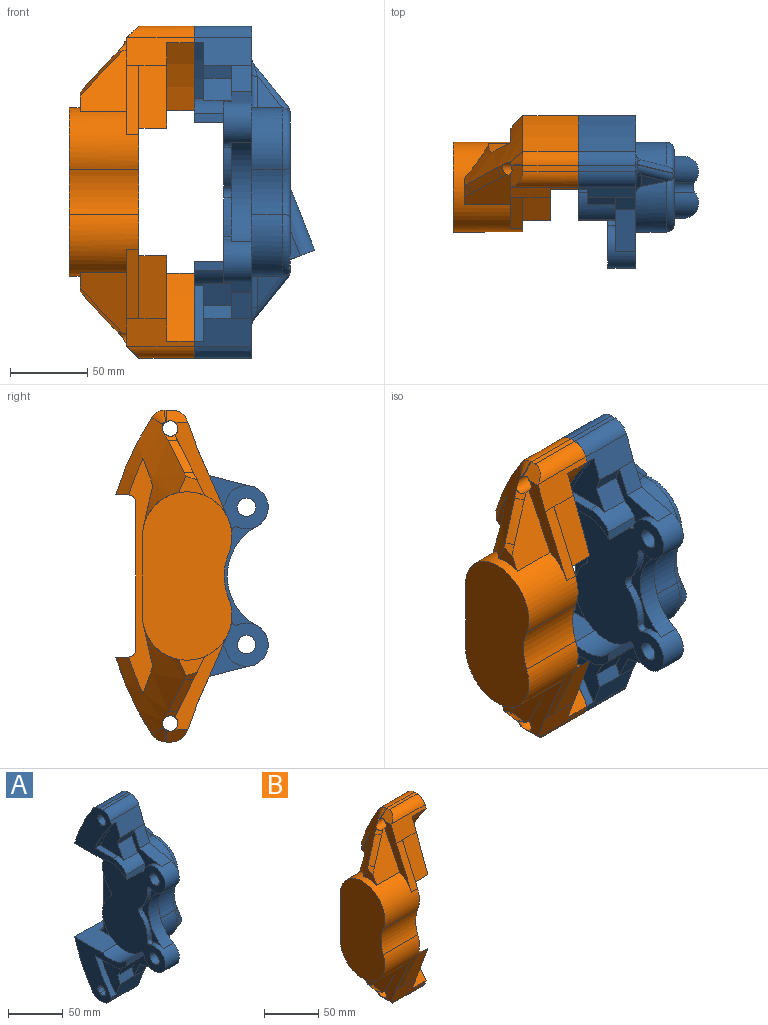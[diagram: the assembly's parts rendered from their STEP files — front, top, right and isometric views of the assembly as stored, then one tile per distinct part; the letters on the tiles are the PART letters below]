
ASSEMBLY  parts=2 mates=1
PART A: 111 faces, bbox 78.4x99.2x215.6 mm
  f0: plane 0.16x0.1mm, normal (1,0,0), area 0mm2, adj f5,f6,f106
  f1: plane 11.19x6.2mm, normal (1,0,0), area 44.8mm2, adj f2,f99,f105,f106
  f2: torus R=24mm, axis (1,0,0), area 416.6mm2, adj f1,f6,f7,f70,f76,f84,f86,f99
  f3: torus R=24mm, axis (1,0,0), area 209mm2, adj f4,f7,f8,f77,f82,f99,f101,f106
  f4: cylinder r=5mm len=4.92mm, axis (0,0.04,-1), area 9.5mm2, adj f3,f5,f77,f87,f106
  f5: cylinder r=5mm len=3.73mm, axis (0,-0.98,-0.19), area 5.6mm2, adj f0,f4,f6,f75,f86,f87,f106
  f6: cylinder r=5mm len=5.52mm, axis (0,0.34,-0.94), area 9.8mm2, adj f0,f2,f5,f86,f106
  f7: plane 90.46x48mm, normal (1,0,0), area 2353.6mm2, adj f2,f3,f78,f79,f80,f81,f82,f83
  f8: cylinder r=29mm len=25.69mm, axis (-1,0,0), area 582.4mm2, adj f3,f9,f71,f77,f89
  f9: plane 215x98.65mm, normal (1,0,0), area 5498.8mm2, adj f8,f10,f18,f19,f20,f21,f22,f23
  f10: cylinder r=29mm len=25.69mm, axis (-1,0,0), area 582.4mm2, adj f9,f71,f74,f80,f98
  f11: plane 37.95x37.12mm, normal (-1,0,0), area 306.6mm2, adj f44,f45,f46,f62,f63,f65,f66,f108
  f12: cylinder r=29mm len=48.75mm, axis (1,0,0), area 296.6mm2, adj f21,f28,f53,f54
  f13: extruded ~36.27x20.87mm, area 251.8mm2, adj f22,f27,f61,f67
  f14: cylinder r=159mm len=36.27mm, axis (-1,0,0), area 251.8mm2, adj f34,f36,f56,f60
  f15: cylinder r=20mm len=24mm, axis (1,0,0), area 348.4mm2, adj f16,f36,f56,f57,f58,f60
  f16: plane 37.95x37.12mm, normal (-1,0,0), area 306.6mm2, adj f15,f40,f41,f42,f57,f58,f59,f109
  f17: plane 64.37x27.62mm, normal (-1,0,0), area 336.7mm2, adj f42,f43,f44,f49,f50,f51,f107,f110
  f18: plane 37x3.51mm, normal (0,0,-1), area 130mm2, adj f9,f19,f26,f27
  f19: extruded ~37x9.16mm, area 400.7mm2, adj f9,f18,f20,f27
  f20: extruded ~50.09x37mm, area 2052.7mm2, adj f9,f19,f21,f27
  f21: plane 37x35.62mm, normal (0,0,1), area 958.8mm2, adj f9,f12,f20,f27,f28,f37,f64
  f22: plane 37x18.15mm, normal (0,-0.94,-0.34), area 621.1mm2, adj f9,f13,f26,f27,f46,f66,f67
  f23: extruded ~37x9.2mm, area 474.9mm2, adj f9,f24,f25,f27
  f24: extruded ~37x9.2mm, area 580.9mm2, adj f9,f23,f25,f27
  f25: extruded ~37x2.72mm, area 106.2mm2, adj f9,f23,f24,f27
  f26: extruded ~37x10.34mm, area 497.3mm2, adj f9,f18,f22,f27
  f27: plane 67.65x62.49mm, normal (-1,0,0), area 1567mm2, adj f13,f18,f19,f20,f21,f22,f23,f24
  f28: plane 105x27.62mm, normal (-1,0,0), area 938.6mm2, adj f12,f21,f29,f37,f38,f39,f52,f53
  f29: plane 37x35.62mm, normal (0,0,-1), area 958.8mm2, adj f9,f28,f30,f36,f39,f52,f55
  f30: cylinder r=185.44mm len=50.09mm, axis (-1,0,0), area 2052.7mm2, adj f9,f29,f31,f36
  f31: cylinder r=11mm len=37mm, axis (-1,0,0), area 400.7mm2, adj f9,f30,f32,f36
  f32: plane 37x3.51mm, normal (0,0,1), area 130mm2, adj f9,f31,f33,f36
  f33: cylinder r=11mm len=37mm, axis (-1,0,0), area 497.2mm2, adj f9,f32,f34,f36
  f34: plane 37x18.15mm, normal (0,-0.94,0.34), area 621.1mm2, adj f9,f14,f33,f36,f40,f59,f60
  f35: cylinder r=5mm len=37mm, axis (-1,0,0), area 1162.4mm2, adj f9,f36
  f36: plane 67.65x62.49mm, normal (-1,0,0), area 1567mm2, adj f14,f15,f29,f30,f31,f32,f33,f34
  f37: cylinder r=5mm len=13mm, axis (-1,0,0), area 102.1mm2, adj f9,f21,f28,f38
  f38: plane 95x13mm, normal (0,1,0), area 1235mm2, adj f9,f28,f37,f39
  f39: cylinder r=5mm len=13mm, axis (-1,0,0), area 102.1mm2, adj f9,f28,f29,f38
  f40: plane 17.18x13mm, normal (0,-0.92,0.4), area 243.9mm2, adj f9,f16,f34,f41
  f41: plane 27.49x13mm, normal (0,-0.24,0.97), area 368.3mm2, adj f9,f16,f40,f42
  f42: cylinder r=14mm len=28mm, axis (-1,0,0), area 780.4mm2, adj f9,f16,f17,f41,f43,f54,f109,f110
  f43: cylinder r=36.6mm len=64.37mm, axis (-1,0,0), area 1022.7mm2, adj f9,f17,f42,f44
  f44: cylinder r=14mm len=28mm, axis (-1,0,0), area 780.4mm2, adj f9,f11,f17,f43,f45,f54,f107,f108
  f45: plane 27.49x13mm, normal (0,-0.24,-0.97), area 368.3mm2, adj f9,f11,f44,f46
  f46: plane 17.18x13mm, normal (0,-0.92,-0.4), area 243.9mm2, adj f9,f11,f22,f45
  f47: cylinder r=6mm len=18mm, axis (-1,0,0), area 678.6mm2, adj f9,f54
  f48: cylinder r=6mm len=18mm, axis (-1,0,0), area 678.6mm2, adj f9,f54
  f49: cylinder r=29mm len=24.78mm, axis (1,0,0), area 138.1mm2, adj f17,f50,f54,f107
  f50: cylinder r=5mm len=7.5mm, axis (1,0,0), area 42.4mm2, adj f17,f49,f51,f54
  f51: cylinder r=29mm len=24.78mm, axis (1,0,0), area 138.1mm2, adj f17,f50,f54,f110
  f52: cylinder r=29mm len=48.75mm, axis (1,0,0), area 296.6mm2, adj f28,f29,f53,f54
  f53: cylinder r=5mm len=7.5mm, axis (1,0,0), area 42.4mm2, adj f12,f28,f52,f54
  f54: plane 117x81.45mm, normal (-1,0,0), area 6213.2mm2, adj f12,f42,f44,f47,f48,f49,f50,f51
  f55: cylinder r=29mm len=32.03mm, axis (1,0,0), area 664.6mm2, adj f29,f36,f54,f57
  f56: plane 23.22x6mm, normal (0,0,1), area 139.3mm2, adj f14,f15,f36,f60
  f57: plane 24x5.92mm, normal (0,-1,0.1), area 142.8mm2, adj f15,f16,f36,f55,f109
  f58: plane 18x14.72mm, normal (0,-0.89,0.46), area 298.1mm2, adj f15,f16,f59,f60
  f59: plane 18x8.45mm, normal (0,-0.95,-0.33), area 160.8mm2, adj f16,f34,f58,f60
  f60: plane 37.79x30.87mm, normal (-1,0,0), area 568.6mm2, adj f14,f15,f34,f56,f58,f59
  f61: plane 23.22x6mm, normal (0,0,-1), area 139.3mm2, adj f13,f27,f62,f67
  f62: cylinder r=20mm len=24mm, axis (1,0,0), area 348.4mm2, adj f11,f27,f61,f63,f65,f67
  f63: plane 24x5.92mm, normal (0,-1,-0.1), area 142.8mm2, adj f11,f27,f62,f64,f108
  f64: cylinder r=29mm len=32.03mm, axis (1,0,0), area 664.6mm2, adj f21,f27,f54,f63
  f65: plane 18x14.72mm, normal (0,-0.89,-0.46), area 298.1mm2, adj f11,f62,f66,f67
  f66: plane 18x8.45mm, normal (0,-0.95,0.33), area 160.8mm2, adj f11,f22,f65,f67
  f67: plane 37.79x30.87mm, normal (-1,0,0), area 568.6mm2, adj f13,f22,f61,f62,f65,f66
  f68: cylinder r=29mm len=39.95mm, axis (-1,0,0), area 1165.7mm2, adj f9,f69,f73,f83,f94
  f69: cylinder r=38.52mm len=29.1mm, axis (-1,0,0), area 596.7mm2, adj f9,f68,f70,f84
  f70: cylinder r=29mm len=39.95mm, axis (-1,0,0), area 1165.7mm2, adj f2,f9,f69,f76,f93
  f71: plane 51x20mm, normal (0,1,0), area 1020mm2, adj f8,f9,f10,f82
  f72: plane 28.79x22.88mm, normal (0.79,0.12,0.6), area 7.1mm2, adj f79,f85,f88,f96
  f73: plane 20.48x16.32mm, normal (0.19,-0.92,0.33), area 175.7mm2, adj f68,f83,f88,f94
  f74: plane 23.64x17.18mm, normal (0.19,0.98,-0.04), area 202.3mm2, adj f10,f78,f80,f85,f98
  f75: plane 28.79x22.88mm, normal (0.79,0.12,-0.6), area 7.1mm2, adj f5,f86,f87,f91
  f76: plane 20.48x16.32mm, normal (0.19,-0.92,-0.33), area 175.7mm2, adj f2,f70,f86,f93
  f77: plane 23.64x17.18mm, normal (0.19,0.98,0.04), area 202.3mm2, adj f3,f4,f8,f87,f89
  f78: cylinder r=5mm len=5.31mm, axis (0,0.04,1), area 16.2mm2, adj f7,f74,f79,f80,f85
  f79: cylinder r=5mm len=3.73mm, axis (0,0.98,-0.19), area 5.6mm2, adj f7,f72,f78,f81,f85,f88
  f80: torus R=24mm, axis (1,0,0), area 241.9mm2, adj f7,f10,f74,f78,f82
  f81: cylinder r=5mm len=6.17mm, axis (0,0.34,0.94), area 13.2mm2, adj f7,f79,f83,f88
  f82: cylinder r=5mm len=51mm, axis (0,0,-1), area 400.6mm2, adj f3,f7,f71,f80
  f83: torus R=24mm, axis (1,0,0), area 457.5mm2, adj f7,f68,f73,f81,f84,f88
  f84: torus R=43.52mm, axis (1,0,0), area 245.4mm2, adj f2,f7,f69,f83
  f85: cylinder r=5mm len=33.13mm, axis (-0.62,0.15,0.77), area 228.6mm2, adj f72,f74,f78,f79,f97
  f86: cylinder r=5mm len=31.42mm, axis (0.62,-0.15,0.77), area 228mm2, adj f2,f5,f6,f75,f76,f92
  f87: cylinder r=5mm len=33.13mm, axis (0.62,-0.15,0.77), area 228.6mm2, adj f4,f5,f75,f77,f90
  f88: cylinder r=5mm len=31.42mm, axis (-0.62,0.15,0.77), area 228mm2, adj f72,f73,f79,f81,f83,f95
  f89: cylinder r=5mm len=27.48mm, axis (0,0.04,-1), area 171.2mm2, adj f8,f9,f77,f90
  f90: bspline ~16.57x8.96mm, area 69.3mm2, adj f9,f87,f89,f91
  f91: cylinder r=5mm len=3.06mm, axis (0,0.98,0.19), area 0.6mm2, adj f9,f75,f90,f92
  f92: bspline ~14.27x13.99mm, area 69.3mm2, adj f9,f86,f91,f93
  f93: cylinder r=5mm len=23.83mm, axis (0,0.34,-0.94), area 154.8mm2, adj f9,f70,f76,f92
  f94: cylinder r=5mm len=23.83mm, axis (0,0.34,0.94), area 154.8mm2, adj f9,f68,f73,f95
  f95: bspline ~12x11.87mm, area 69.3mm2, adj f9,f88,f94,f96
  f96: cylinder r=5mm len=3.06mm, axis (0,-0.98,0.19), area 0.6mm2, adj f9,f72,f95,f97
  f97: bspline ~13.93x7.79mm, area 69.3mm2, adj f9,f85,f96,f98
  f98: cylinder r=5mm len=27.48mm, axis (0,0.04,1), area 171.2mm2, adj f9,f10,f74,f97
  f99: plane 40.41x19.05mm, normal (0.36,0,-0.93), area 666.4mm2, adj f1,f2,f3,f100,f101,f102,f103,f104
  f100: plane 19.86x7.93mm, normal (0,-1,0), area 64.9mm2, adj f2,f7,f99,f102
  f101: plane 20.44x8.51mm, normal (0,1,0), area 64.9mm2, adj f3,f7,f99,f103
  f102: cylinder r=10mm len=44.41mm, axis (0.36,0,-0.93), area 842.7mm2, adj f7,f99,f100,f104
  f103: cylinder r=10mm len=44.41mm, axis (0.36,0,-0.93), area 842.7mm2, adj f7,f99,f101,f104
  f104: cylinder r=5mm len=35.1mm, axis (-0.36,0,0.93), area 255.4mm2, adj f7,f99,f102,f103
  f105: cylinder r=10mm len=14.17mm, axis (-0.36,0,0.93), area 62.4mm2, adj f1,f2,f99
  f106: cylinder r=10mm len=14.17mm, axis (-0.36,0,0.93), area 67.8mm2, adj f0,f1,f2,f3,f4,f5,f6,f99
  f107: cylinder r=3mm len=5mm, axis (-1,0,0), area 31.1mm2, adj f17,f44,f49,f54
  f108: cylinder r=3mm len=5mm, axis (-1,0,0), area 22.3mm2, adj f11,f44,f54,f63
  f109: cylinder r=3mm len=5mm, axis (-1,0,0), area 22.3mm2, adj f16,f42,f54,f57
  f110: cylinder r=3mm len=5mm, axis (-1,0,0), area 31.1mm2, adj f17,f42,f51,f54
PART B: 64 faces, bbox 84.4x82.9x218.4 mm
  f0: cylinder r=11mm len=43.24mm, axis (-1,0,0), area 532.4mm2, adj f1,f5,f6,f7
  f1: plane 36x3.51mm, normal (0,0,1), area 126.5mm2, adj f0,f4,f5,f7
  f2: bspline ~8.02x8mm, area 8mm2, adj f4,f5,f11,f13
  f3: plane 2.19x1.88mm, normal (-1,0,0), area 1.3mm2, adj f11,f12,f13
  f4: cylinder r=11mm len=36mm, axis (-1,0,0), area 389.9mm2, adj f1,f2,f7,f13,f14
  f5: plane 17.52x11.39mm, normal (-0.71,0,0.71), area 122.3mm2, adj f0,f1,f2,f6,f11,f17
  f6: plane 44x18.15mm, normal (0,-0.94,0.34), area 569.2mm2, adj f0,f5,f7,f8,f9,f17,f20,f21
  f7: plane 55x47.67mm, normal (1,0,0), area 1278.3mm2, adj f0,f1,f4,f6,f8,f11,f14,f22
  f8: cylinder r=159mm len=44.24mm, axis (-1,0,0), area 909mm2, adj f6,f7,f9,f22
  f9: plane 55.33x44.24mm, normal (1,0,0), area 1004.2mm2, adj f6,f8,f20,f22,f23
  f10: bspline ~8.32x7.13mm, area 33.1mm2, adj f11,f16,f18,f32
  f11: cylinder r=5mm len=49.27mm, axis (-1,0,0), area 1424.7mm2, adj f2,f3,f5,f7,f10,f12,f17,f18
  f12: plane 0.87x0.68mm, normal (0,-0.63,0.77), area 0.4mm2, adj f3,f11,f32
  f13: cone r=7mm half-angle=45deg, axis (1,0,0), area 69.9mm2, adj f2,f3,f4,f32
  f14: cylinder r=185.44mm len=50.09mm, axis (-1,0,0), area 1997.2mm2, adj f4,f7,f22,f32
  f15: bspline ~8.39x7.27mm, area 33.6mm2, adj f16,f18,f19,f32
  f16: bspline ~22.13x21.09mm, area 199.9mm2, adj f10,f15,f18,f32
  f17: plane 62.33x34.59mm, normal (-1,0,0), area 485.2mm2, adj f5,f6,f11,f18,f21,f35
  f18: plane 39.28x30mm, normal (0,-0.9,0.44), area 872.3mm2, adj f10,f11,f15,f16,f17,f19,f35
  f19: plane 17.03x12.56mm, normal (-1,0,0), area 111.8mm2, adj f15,f18,f32,f35
  f20: plane 40.7x18mm, normal (0,-0.94,0.35), area 780.9mm2, adj f6,f9,f23,f38
  f21: plane 44.95x19.76mm, normal (0,-0.92,0.4), area 392.8mm2, adj f6,f17,f35,f38
  f22: plane 46.32x43.78mm, normal (0,0,-1), area 1290.1mm2, adj f7,f8,f9,f14,f23,f31,f32,f38
  f23: cylinder r=27mm len=21.81mm, axis (-1,0,0), area 457mm2, adj f9,f20,f22,f38
  f24: plane 40.7x18mm, normal (0,-0.94,-0.35), area 780.9mm2, adj f27,f38,f39,f40
  f25: plane 36x3.51mm, normal (0,0,-1), area 126.5mm2, adj f26,f42,f43,f44
  f26: cylinder r=11mm len=43.24mm, axis (-1,0,0), area 532.4mm2, adj f25,f27,f43,f44
  f27: plane 44x18.15mm, normal (0,-0.94,-0.34), area 569.2mm2, adj f24,f26,f28,f40,f41,f43,f44,f47
  f28: plane 44.95x19.76mm, normal (0,-0.92,-0.4), area 392.8mm2, adj f27,f38,f47,f48
  f29: cylinder r=38.52mm len=45mm, axis (-1,0,0), area 1342.7mm2, adj f30,f35,f38,f48
  f30: plane 109.55x58.28mm, normal (-1,0,0), area 5466.4mm2, adj f29,f35,f36,f48
  f31: cylinder r=5mm len=8mm, axis (-1,0,0), area 62.8mm2, adj f22,f32,f37,f38,f51
  f32: cone r=181.44mm half-angle=45deg, axis (1,0,0), area 1742mm2, adj f10,f11,f12,f13,f14,f15,f16,f19
  f33: plane 17.26x12.62mm, normal (0,0.94,-0.34), area 117.6mm2, adj f32,f34,f51
  f34: plane 27.06x14.58mm, normal (0,0.98,0.22), area 384.5mm2, adj f32,f33,f35,f51
  f35: cylinder r=29mm len=58mm, axis (-1,0,0), area 2789.2mm2, adj f17,f18,f19,f21,f29,f30,f32,f34
  f36: plane 51x37mm, normal (0,1,0), area 1887mm2, adj f30,f35,f48,f51
  f37: plane 95x8mm, normal (0,1,0), area 760mm2, adj f31,f38,f51,f52
  f38: plane 164.23x67.34mm, normal (1,0,0), area 6173mm2, adj f20,f21,f22,f23,f24,f28,f29,f31
  f39: cylinder r=27mm len=21.81mm, axis (-1,0,0), area 457mm2, adj f24,f38,f40,f53
  f40: plane 55.33x44.24mm, normal (1,0,0), area 1004.2mm2, adj f24,f27,f39,f41,f53
  f41: cylinder r=159mm len=44.24mm, axis (-1,0,0), area 909mm2, adj f27,f40,f43,f53
  f42: cylinder r=11mm len=36mm, axis (-1,0,0), area 389.9mm2, adj f25,f43,f45,f54,f55
  f43: plane 55x47.67mm, normal (1,0,0), area 1278.3mm2, adj f25,f26,f27,f41,f42,f53,f54,f57
  f44: plane 17.42x11.3mm, normal (-0.71,0,-0.71), area 122.3mm2, adj f25,f26,f27,f45,f47,f57
  f45: bspline ~8.02x8mm, area 8mm2, adj f42,f44,f55,f57
  f46: plane 2.19x1.88mm, normal (-1,0,0), area 1.3mm2, adj f55,f56,f57
  f47: plane 62.33x34.59mm, normal (-1,0,0), area 485.2mm2, adj f27,f28,f44,f48,f57,f60
  f48: cylinder r=29mm len=58mm, axis (-1,0,0), area 2783.6mm2, adj f28,f29,f30,f36,f38,f47,f49,f51
  f49: plane 27.06x14.58mm, normal (0,0.98,-0.22), area 384.5mm2, adj f48,f50,f51,f62
  f50: plane 17.26x12.62mm, normal (0,0.94,0.34), area 117.6mm2, adj f49,f51,f62
  f51: plane 152.2x15.54mm, normal (-1,0,0), area 991.4mm2, adj f31,f32,f33,f34,f35,f36,f37,f48
  f52: cylinder r=5mm len=8mm, axis (-1,0,0), area 62.8mm2, adj f37,f38,f51,f53,f62
  f53: plane 46.32x43.78mm, normal (0,0,1), area 1290.1mm2, adj f38,f39,f40,f41,f43,f52,f54,f62
  f54: cylinder r=185.44mm len=50.09mm, axis (-1,0,0), area 1997.2mm2, adj f42,f43,f53,f62
  f55: cone r=7mm half-angle=45deg, axis (1,0,0), area 69.9mm2, adj f42,f45,f46,f62
  f56: plane 0.87x0.68mm, normal (0,-0.63,-0.77), area 0.4mm2, adj f46,f57,f62
  f57: cylinder r=5mm len=49.27mm, axis (-1,0,0), area 1425.1mm2, adj f43,f44,f45,f46,f47,f56,f58,f60
  f58: bspline ~8.32x7.13mm, area 39.6mm2, adj f57,f59,f60,f62
  f59: bspline ~22.13x21.09mm, area 199.9mm2, adj f58,f60,f62,f63
  f60: plane 39.28x30mm, normal (0,-0.9,-0.44), area 872.3mm2, adj f47,f48,f57,f58,f59,f61,f63
  f61: plane 17.03x12.56mm, normal (-1,0,0), area 111.8mm2, adj f48,f60,f62,f63
  f62: cone r=181.44mm half-angle=45deg, axis (1,0,0), area 1737mm2, adj f48,f49,f50,f51,f52,f53,f54,f55
  f63: bspline ~8.39x7.27mm, area 33.6mm2, adj f59,f60,f61,f62
PLACE A t=(-42.32,-33.75,5.01)mm fixed
PLACE B t=(-42.32,-33.75,5.01)mm
MATE fastened A.f36 <-> B.f7  axis (-1,0,0) through (-79.12,12.45,32.01)mm
